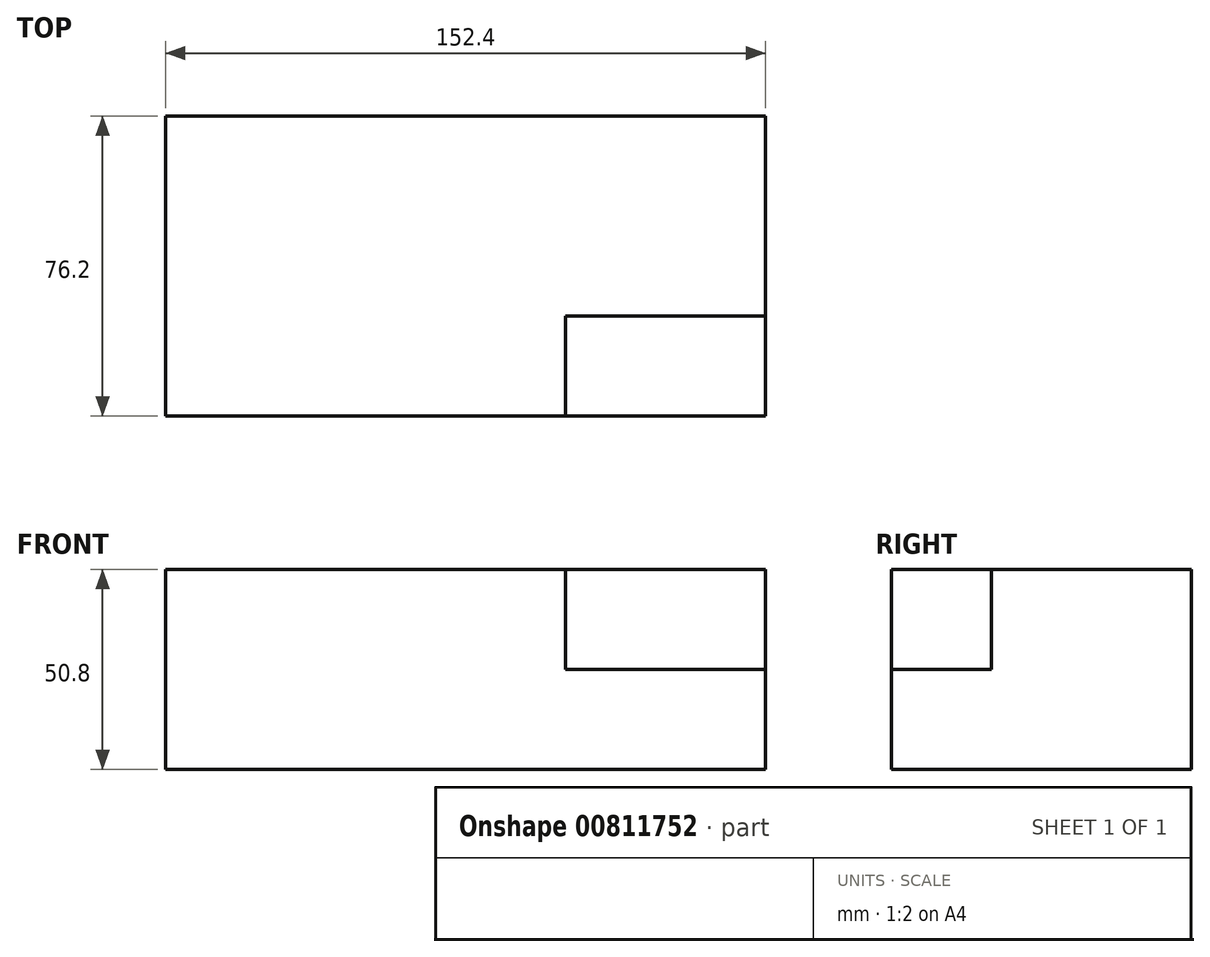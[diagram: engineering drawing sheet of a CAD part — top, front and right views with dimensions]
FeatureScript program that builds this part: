
annotation { "Feature Type Name" : "Feature", "Feature Type Description" : "" }
export const myFeature = defineFeature(function(context is Context, id is Id, definition is map)
    precondition{}
    {
        {
            var Q0;
            Q0=qCreatedBy(makeId("Top.planeOp"),FACE);
            var sketch = newSketch(context, id + "F0", { "sketchPlane" : qUnion([Q0])});
            skLineSegment(sketch, "E0", {"start": v(0, 0) * mm, "end": v(152.4, 0) * mm});
            skLineSegment(sketch, "E1", {"start": v(152.4, 0) * mm, "end": v(152.4, 76.2) * mm});
            skLineSegment(sketch, "E2", {"start": v(152.4, 76.2) * mm, "end": v(0, 76.2) * mm});
            skLineSegment(sketch, "E3", {"start": v(0, 0) * mm, "end": v(0, 76.2) * mm});
            skSolve(sketch);
        }
        {
            var Q0;
            Q0=makeQuery(id+"F0.imprint","IMPRINT",FACE,{"disambiguationData":[TD([[makeQuery(id+"F0.imprint","IMPRINT",EDGE,{"derivedFrom":sQuery(id+"F0.wireOp",EDGE,"E0")}),1.0]])]});
            extrude(context, id + "F1", {"entities" : qUnion([Q0]), "depth" : 50.8 * mm, "offsetDistance" : 25.4 * mm});
        }
        {
            var Q0;
            Q0=makeQuery(id+"F1.opExtrude","SWEPT_FACE",FACE,{"disambiguationData":[OSD([sQuery(id+"F0.wireOp",EDGE,"E0")])]});
            var sketch = newSketch(context, id + "F2", { "sketchPlane" : qUnion([Q0])});
            skLineSegment(sketch, "E4", {"start": v(152.4, 50.8) * mm, "end": v(101.6, 50.8) * mm});
            skLineSegment(sketch, "E5", {"start": v(101.6, 50.8) * mm, "end": v(101.6, 25.4) * mm});
            skLineSegment(sketch, "E6", {"start": v(101.6, 25.4) * mm, "end": v(152.4, 25.4) * mm});
            skLineSegment(sketch, "E7", {"start": v(152.4, 25.4) * mm, "end": v(152.4, 50.8) * mm});
            skSolve(sketch);
        }
        {
            var Q0;
            Q0=makeQuery(id+"F2.imprint","IMPRINT",FACE,{"disambiguationData":[TD([[makeQuery(id+"F2.imprint","IMPRINT",EDGE,{"derivedFrom":sQuery(id+"F2.wireOp",EDGE,"E4")}),-1.0]])]});
            extrude(context, id + "F3", {"entities" : qUnion([Q0]), "operationType" : NewBodyOperationType.REMOVE, "oppositeDirection" : true, "depth" : 25.4 * mm, "offsetDistance" : 25.4 * mm});
        }
    });
